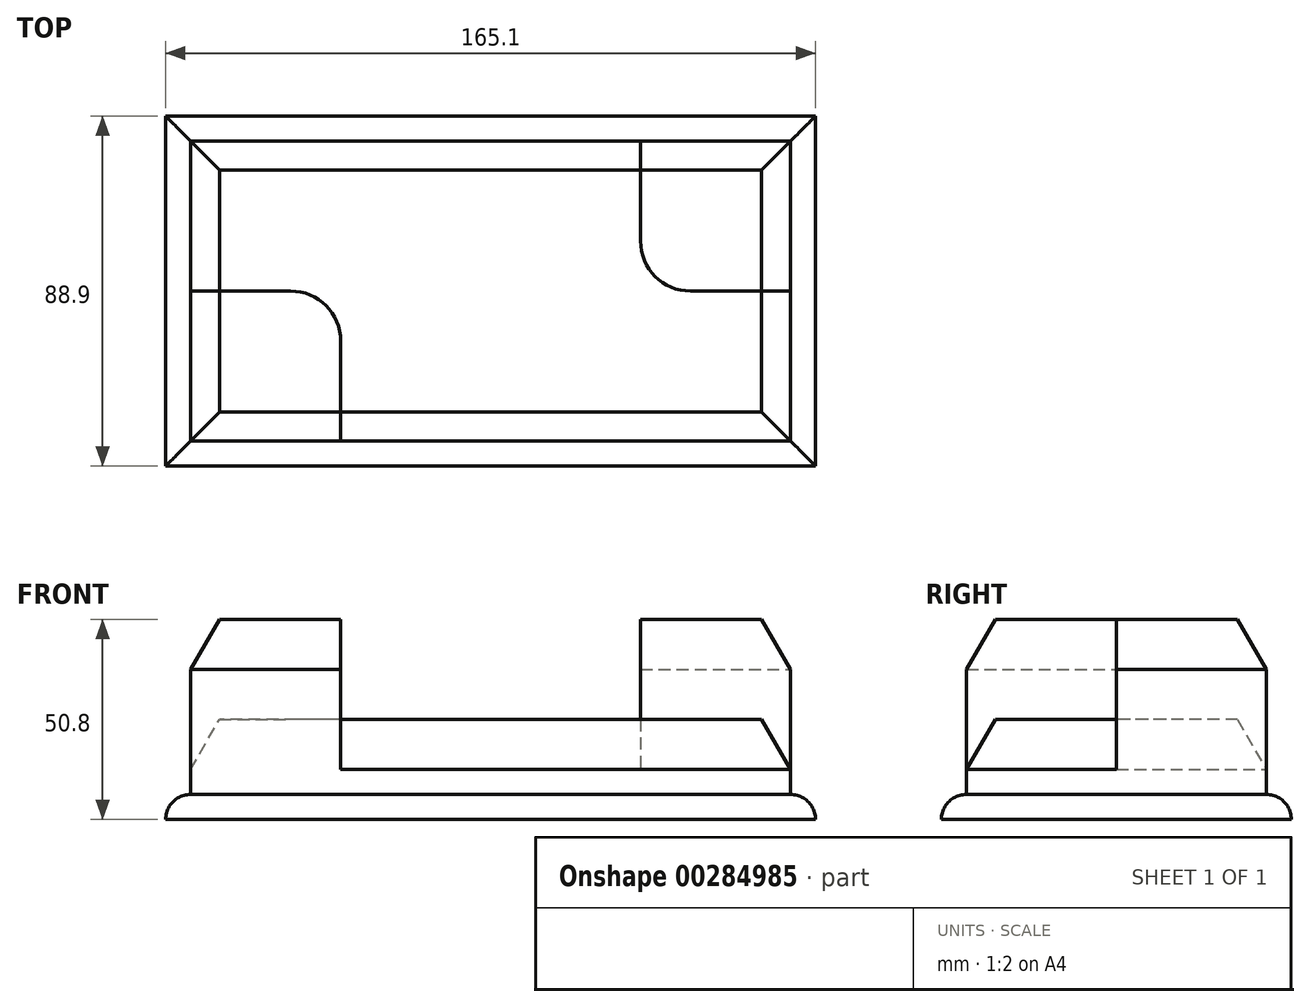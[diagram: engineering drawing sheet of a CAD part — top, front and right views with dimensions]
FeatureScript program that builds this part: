
annotation { "Feature Type Name" : "Feature", "Feature Type Description" : "" }
export const myFeature = defineFeature(function(context is Context, id is Id, definition is map)
    precondition{}
    {
        {
            var Q0;
            Q0=qCreatedBy(makeId("Top.planeOp"),FACE);
            var sketch = newSketch(context, id + "F0", { "sketchPlane" : qUnion([Q0])});
            skLineSegment(sketch, "E0", {"start": v(-48.13, 68.15) * mm, "end": v(116.97, 68.15) * mm});
            skLineSegment(sketch, "E1", {"start": v(116.97, 68.15) * mm, "end": v(116.97, -20.75) * mm});
            skLineSegment(sketch, "E2", {"start": v(116.97, -20.75) * mm, "end": v(-48.13, -20.75) * mm});
            skLineSegment(sketch, "E3", {"start": v(-48.13, -20.75) * mm, "end": v(-48.13, 68.15) * mm});
            skLineSegment(sketch, "E4.0", {"start": v(-41.78, 61.8) * mm, "end": v(110.62, 61.8) * mm});
            skLineSegment(sketch, "E5.0", {"start": v(-41.78, -14.4) * mm, "end": v(-41.78, 61.8) * mm});
            skLineSegment(sketch, "E6.0", {"start": v(110.62, -14.4) * mm, "end": v(-41.78, -14.4) * mm});
            skLineSegment(sketch, "E7.0", {"start": v(110.62, 61.8) * mm, "end": v(110.62, -14.4) * mm});
            skLineSegment(sketch, "E8", {"start": v(-41.78, 23.7) * mm, "end": v(-16.38, 23.7) * mm});
            skPoint(sketch, "E8.endSnap0", {"position": v(-41.78, 23.7) * mm});
            skLineSegment(sketch, "E9", {"start": v(-3.68, 11) * mm, "end": v(-3.68, -14.4) * mm});
            skLineSegment(sketch, "E10", {"start": v(110.62, 23.7) * mm, "end": v(85.22, 23.7) * mm});
            skLineSegment(sketch, "E11", {"start": v(72.52, 61.8) * mm, "end": v(72.52, 36.4) * mm});
            skArc(sketch, "E12.filletArc", {"start": v(-3.68, 11) * mm, "mid": v(-7.4, 19.98) * mm, "end": v(-16.38, 23.7) * mm});
            skArc(sketch, "E13.filletArc", {"start": v(72.52, 36.4) * mm, "mid": v(76.24, 27.42) * mm, "end": v(85.22, 23.7) * mm});
            skSolve(sketch);
        }
        {
            var Q0;
            Q0 = qSketchRegion(id + "F0", true);
            extrude(context, id + "F1", {"entities" : qUnion([Q0]), "depth" : 6.35 * mm});
        }
        {
            var Q0;
            {var subQ8=sQuery(id+"F0.wireOp",EDGE,"E8");Q0=makeQuery(id+"F0.imprint","IMPRINT",FACE,{"disambiguationData":[TD([[makeQuery(id+"F0.imprint","IMPRINT",EDGE,{"derivedFrom":subQ8}),1.0]])]});}
            extrude(context, id + "F2", {"entities" : qUnion([Q0]), "operationType" : NewBodyOperationType.ADD, "depth" : 25.4 * mm});
        }
        {
            var Q0;
            {var subQ1=sQuery(id+"F0.wireOp",EDGE,"E8");Q0=makeQuery(id+"F0.imprint","IMPRINT",FACE,{"disambiguationData":[TD([[makeQuery(id+"F0.imprint","IMPRINT",EDGE,{"derivedFrom":subQ1}),-1.0]])]});}
            var Q1;
            {var subQ0=sQuery(id+"F0.wireOp",EDGE,"E10");Q1=makeQuery(id+"F0.imprint","IMPRINT",FACE,{"disambiguationData":[TD([[makeQuery(id+"F0.imprint","IMPRINT",EDGE,{"derivedFrom":subQ0}),-1.0]])]});}
            extrude(context, id + "F3", {"entities" : qUnion([Q0, Q1]), "operationType" : NewBodyOperationType.ADD, "depth" : 50.8 * mm});
        }
        {
            var Q0;
            Q0=makeQuery(id+"F1.opExtrude","CAP_EDGE",EDGE,{"disambiguationData":[OSD([sQuery(id+"F0.wireOp",EDGE,"E2")])],"isStart":false});
            var Q1;
            Q1=makeQuery(id+"F1.opExtrude","CAP_EDGE",EDGE,{"disambiguationData":[OSD([sQuery(id+"F0.wireOp",EDGE,"E1")])],"isStart":false});
            var Q2;
            Q2=makeQuery(id+"F1.opExtrude","CAP_EDGE",EDGE,{"disambiguationData":[OSD([sQuery(id+"F0.wireOp",EDGE,"E3")])],"isStart":false});
            var Q3;
            Q3=makeQuery(id+"F1.opExtrude","CAP_EDGE",EDGE,{"disambiguationData":[OSD([sQuery(id+"F0.wireOp",EDGE,"E0")])],"isStart":false});
            fillet(context, id + "F4", {"entities" : qUnion([Q0, Q1, Q2, Q3]), "radius" : 6.35 * mm, "tangentPropagation" : true, "allowEdgeOverflow" : false});
        }
        {
            var Q0;
            Q0=makeQuery(id+"F2.opExtrude","CAP_EDGE",EDGE,{"disambiguationData":[OSD([sQuery(id+"F0.wireOp",EDGE,"E6.0")])],"isStart":false});
            var Q1;
            Q1=makeQuery(id+"F2.opExtrude","CAP_EDGE",EDGE,{"disambiguationData":[OSD([sQuery(id+"F0.wireOp",EDGE,"E7.0")])],"isStart":false});
            var Q2;
            Q2=makeQuery(id+"F3.opExtrude","CAP_EDGE",EDGE,{"disambiguationData":[OSD([sQuery(id+"F0.wireOp",EDGE,"E7.0")])],"isStart":false});
            var Q3;
            Q3=makeQuery(id+"F3.opExtrude","CAP_EDGE",EDGE,{"disambiguationData":[OSD([sQuery(id+"F0.wireOp",EDGE,"E4.0")])],"isStart":false});
            var Q4;
            Q4=makeQuery(id+"F3.opExtrude","CAP_EDGE",EDGE,{"disambiguationData":[OSD([sQuery(id+"F0.wireOp",EDGE,"E6.0")])],"isStart":false});
            var Q5;
            Q5=makeQuery(id+"F3.opExtrude","CAP_EDGE",EDGE,{"disambiguationData":[OSD([sQuery(id+"F0.wireOp",EDGE,"E5.0")])],"isStart":false});
            var Q6;
            Q6=makeQuery(id+"F2.opExtrude","CAP_EDGE",EDGE,{"disambiguationData":[OSD([sQuery(id+"F0.wireOp",EDGE,"E4.0")])],"isStart":false});
            var Q7;
            Q7=makeQuery(id+"F2.opExtrude","CAP_EDGE",EDGE,{"disambiguationData":[OSD([sQuery(id+"F0.wireOp",EDGE,"E5.0")])],"isStart":false});
            chamfer(context, id + "F5", {"entities" : qUnion([Q0, Q1, Q2, Q3, Q4, Q5, Q6, Q7]), "chamferType" : ChamferType.OFFSET_ANGLE, "width" : 12.7 * mm, "oppositeDirection" : false, "angle" : 30 * degree, "tangentPropagation" : true});
        }
    });
